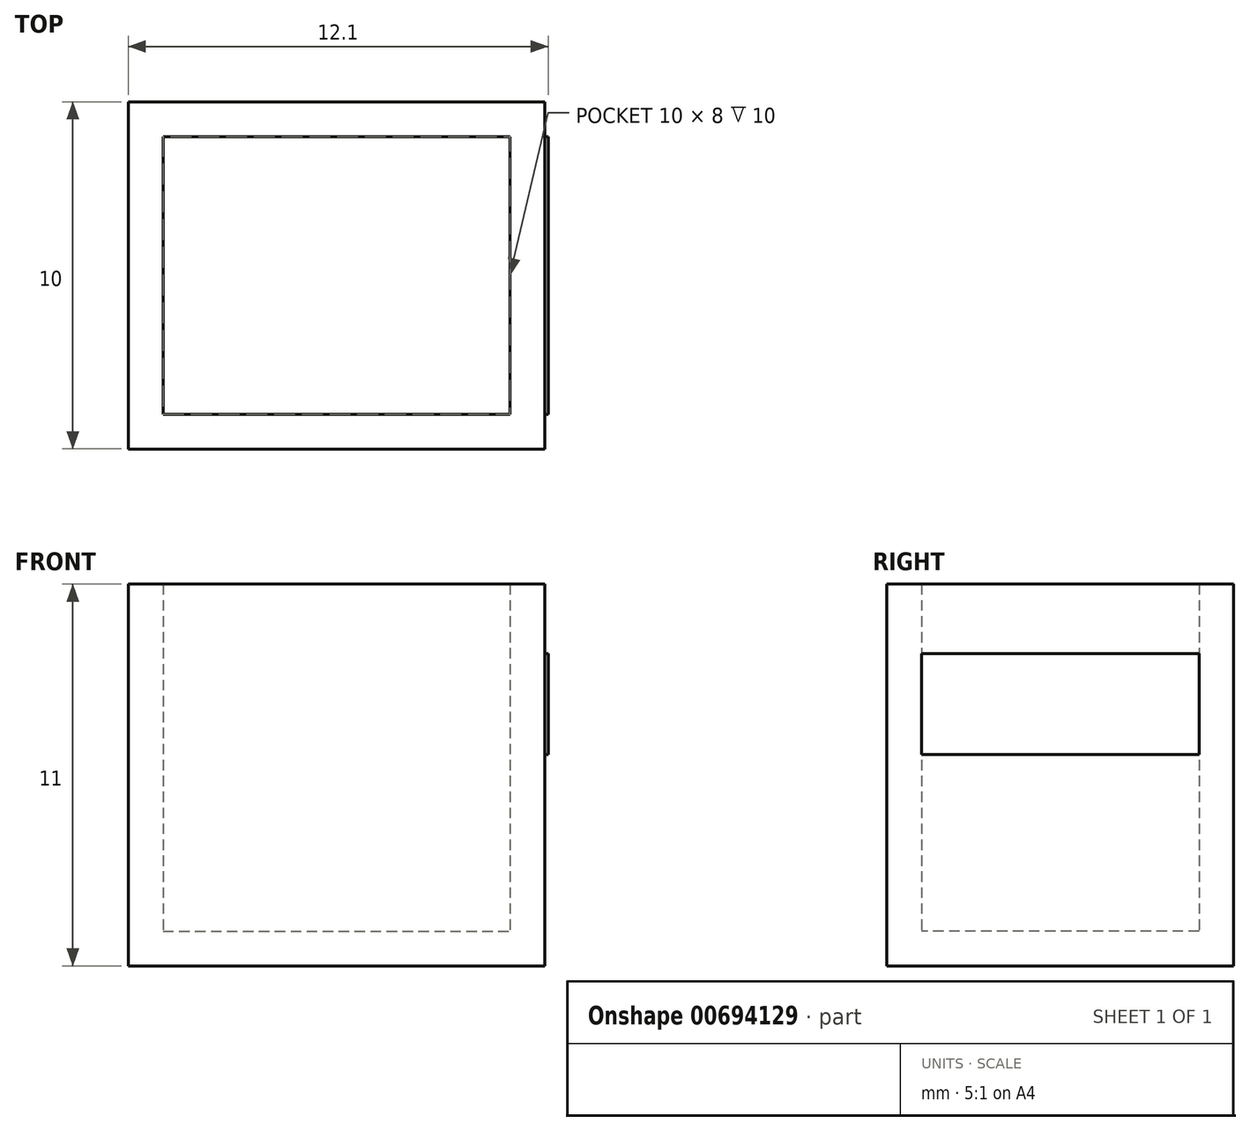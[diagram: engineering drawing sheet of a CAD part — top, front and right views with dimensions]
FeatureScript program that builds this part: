
annotation { "Feature Type Name" : "Feature", "Feature Type Description" : "" }
export const myFeature = defineFeature(function(context is Context, id is Id, definition is map)
    precondition{}
    {
        {
            var Q0;
            Q0=qCreatedBy(makeId("Top.planeOp"),FACE);
            var sketch = newSketch(context, id + "F0", { "sketchPlane" : qUnion([Q0])});
            skLineSegment(sketch, "E0.bottom", {"start": v(-49.99, 5.6) * mm, "end": v(-39.99, 5.6) * mm});
            skLineSegment(sketch, "E0.top", {"start": v(-49.99, -2.4) * mm, "end": v(-39.99, -2.4) * mm});
            skLineSegment(sketch, "E0.left", {"start": v(-49.99, 5.6) * mm, "end": v(-49.99, -2.4) * mm});
            skLineSegment(sketch, "E0.right", {"start": v(-39.99, 5.6) * mm, "end": v(-39.99, -2.4) * mm});
            skSolve(sketch);
        }
        {
            var Q0;
            Q0=makeQuery(id+"F0.imprint","IMPRINT",FACE,{"disambiguationData":[TD([[makeQuery(id+"F0.imprint","IMPRINT",EDGE,{"derivedFrom":sQuery(id+"F0.wireOp",EDGE,"E0.bottom")}),-1.0]])]});
            extrude(context, id + "F1", {"entities" : qUnion([Q0]), "depth" : 10 * mm, "offsetDistance" : 25 * mm});
        }
        {
            var Q0;
            Q0=makeQuery(id+"F1.opExtrude","CAP_FACE",FACE,{"disambiguationData":[OSD([sQuery(id+"F0.wireOp",EDGE,"E0.bottom"),sQuery(id+"F0.wireOp",EDGE,"E0.top"),sQuery(id+"F0.wireOp",EDGE,"E0.left"),sQuery(id+"F0.wireOp",EDGE,"E0.right")])],"isStart":false});
            shell(context, id + "F2", {"entities" : qUnion([Q0]), "thickness" : 1 * mm, "oppositeDirection" : true});
        }
        {
            var Q0;
            Q0=makeQuery(id+"F1.opExtrude","SWEPT_FACE",FACE,{"disambiguationData":[OSD([sQuery(id+"F0.wireOp",EDGE,"E0.right")])]});
            var sketch = newSketch(context, id + "F3", { "sketchPlane" : qUnion([Q0])});
            skLineSegment(sketch, "E1.0.0", {"start": v(-3.4, -1) * mm, "end": v(6.6, -1) * mm});
            skLineSegment(sketch, "E1.0.1", {"start": v(6.6, -1) * mm, "end": v(6.6, 10) * mm});
            skLineSegment(sketch, "E1.0.2", {"start": v(6.6, 10) * mm, "end": v(-3.4, 10) * mm});
            skLineSegment(sketch, "E1.0.3", {"start": v(-3.4, 10) * mm, "end": v(-3.4, -1) * mm});
            skLineSegment(sketch, "E2.bottom", {"start": v(-2.4, 8) * mm, "end": v(5.6, 8) * mm});
            skLineSegment(sketch, "E2.top", {"start": v(-2.4, 5.1) * mm, "end": v(5.6, 5.1) * mm});
            skLineSegment(sketch, "E2.left", {"start": v(-2.4, 8) * mm, "end": v(-2.4, 5.1) * mm});
            skLineSegment(sketch, "E2.right", {"start": v(5.6, 8) * mm, "end": v(5.6, 5.1) * mm});
            skSolve(sketch);
        }
        {
            var Q0;
            Q0=makeQuery(id+"F3.imprint","IMPRINT",FACE,{"disambiguationData":[TD([[makeQuery(id+"F3.imprint","IMPRINT",EDGE,{"derivedFrom":sQuery(id+"F3.wireOp",EDGE,"E2.bottom")}),-1.0]])]});
            extrude(context, id + "F4", {"entities" : qUnion([Q0]), "operationType" : NewBodyOperationType.ADD, "depth" : 0.1 * mm, "offsetDistance" : 25 * mm});
        }
    });
